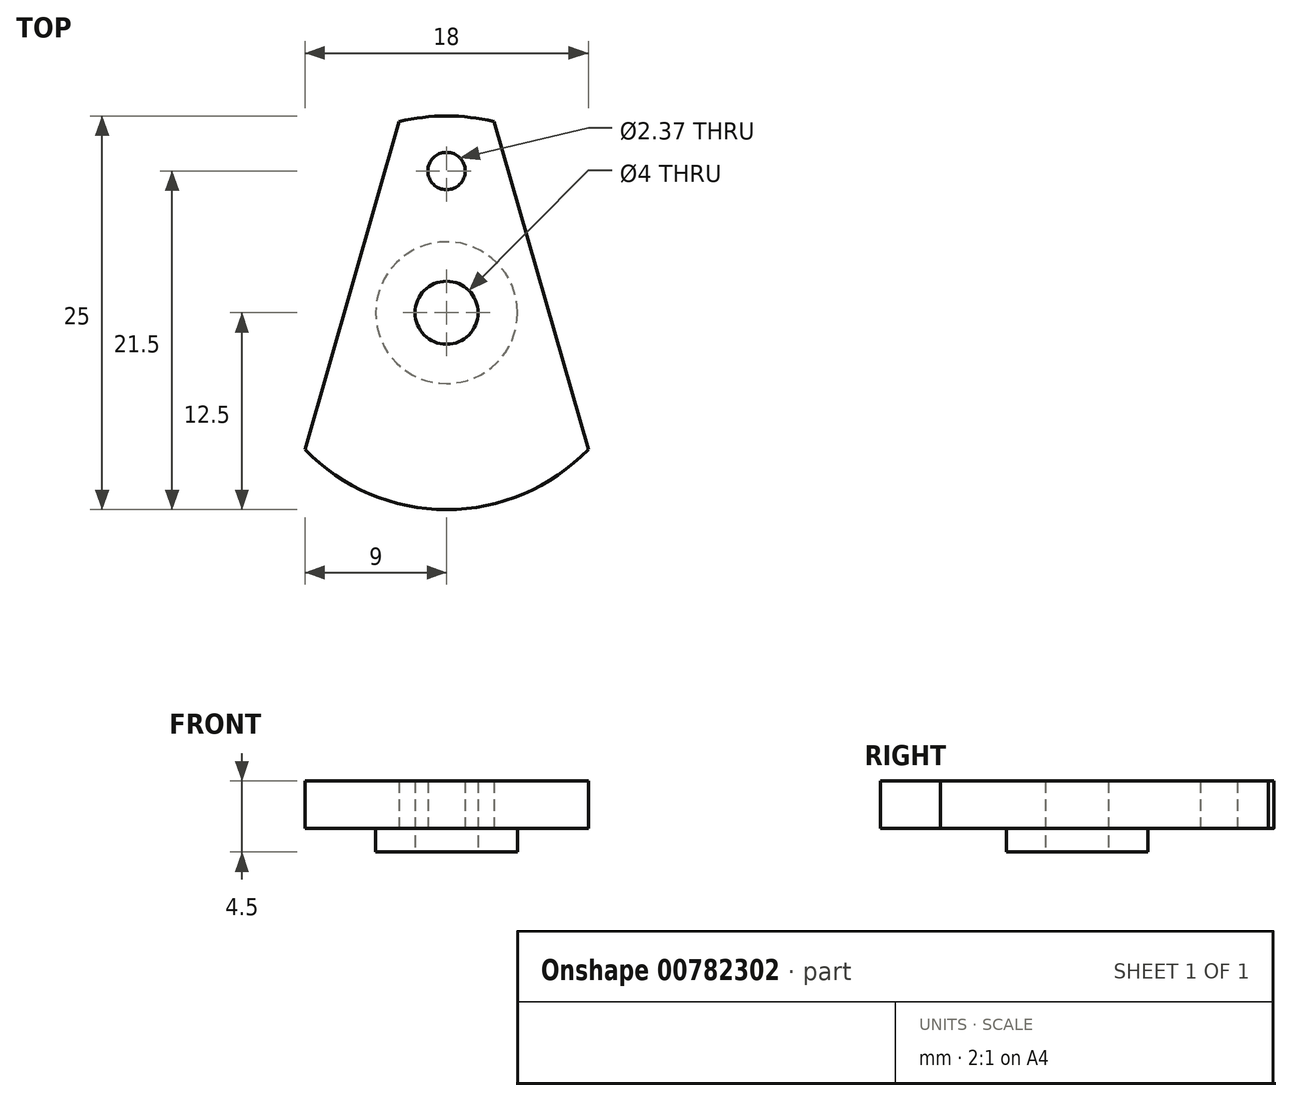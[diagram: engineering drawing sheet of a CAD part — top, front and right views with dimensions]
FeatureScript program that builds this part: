
annotation { "Feature Type Name" : "Feature", "Feature Type Description" : "" }
export const myFeature = defineFeature(function(context is Context, id is Id, definition is map)
    precondition{}
    {
        {
            var Q0;
            Q0=qCreatedBy(makeId("Top.planeOp"),FACE);
            var sketch = newSketch(context, id + "F0", { "sketchPlane" : qUnion([Q0])});
            skArc(sketch, "E0", {"start": v(3, 12.13) * mm, "mid": v(0, 12.5) * mm, "end": v(-3, 12.13) * mm});
            skLineSegment(sketch, "E1", {"start": v(3, 12.13) * mm, "end": v(9, -8.67) * mm});
            skPoint(sketch, "E2.orphan", {"position": v(3, 15.76) * mm});
            skLineSegment(sketch, "E3.MirrorCS", {"start": v(-3, 12.13) * mm, "end": v(-9, -8.67) * mm});
            skArc(sketch, "E4.trimOffspring", {"start": v(-9, -8.67) * mm, "mid": v(0, -12.5) * mm, "end": v(9, -8.67) * mm});
            skCircle(sketch, "E5", {"center": v(0, 0) * mm, "radius": 2 * mm});
            skCircle(sketch, "E6", {"center": v(0, 0) * mm, "radius": 4.5 * mm});
            skCircle(sketch, "E7", {"center": v(0, 9) * mm, "radius": 1.19 * mm});
            skSolve(sketch);
        }
        {
            var Q0;
            Q0=makeQuery(id+"F0.imprint","IMPRINT",FACE,{"disambiguationData":[TD([[makeQuery(id+"F0.imprint","IMPRINT",EDGE,{"derivedFrom":sQuery(id+"F0.wireOp",EDGE,"E0")}),1.0]])]});
            var Q1;
            Q1=makeQuery(id+"F0.imprint","IMPRINT",FACE,{"disambiguationData":[TD([[makeQuery(id+"F0.imprint","IMPRINT",EDGE,{"derivedFrom":sQuery(id+"F0.wireOp",EDGE,"E5")}),-1.0]])]});
            extrude(context, id + "F1", {"entities" : qUnion([Q0, Q1]), "depth" : 3 * mm, "offsetDistance" : 25 * mm});
        }
        {
            var Q0;
            Q0=makeQuery(id+"F0.imprint","IMPRINT",FACE,{"disambiguationData":[TD([[makeQuery(id+"F0.imprint","IMPRINT",EDGE,{"derivedFrom":sQuery(id+"F0.wireOp",EDGE,"E5")}),-1.0]])]});
            extrude(context, id + "F2", {"entities" : qUnion([Q0]), "operationType" : NewBodyOperationType.ADD, "oppositeDirection" : true, "depth" : 1.5 * mm, "offsetDistance" : 25 * mm});
        }
    });
